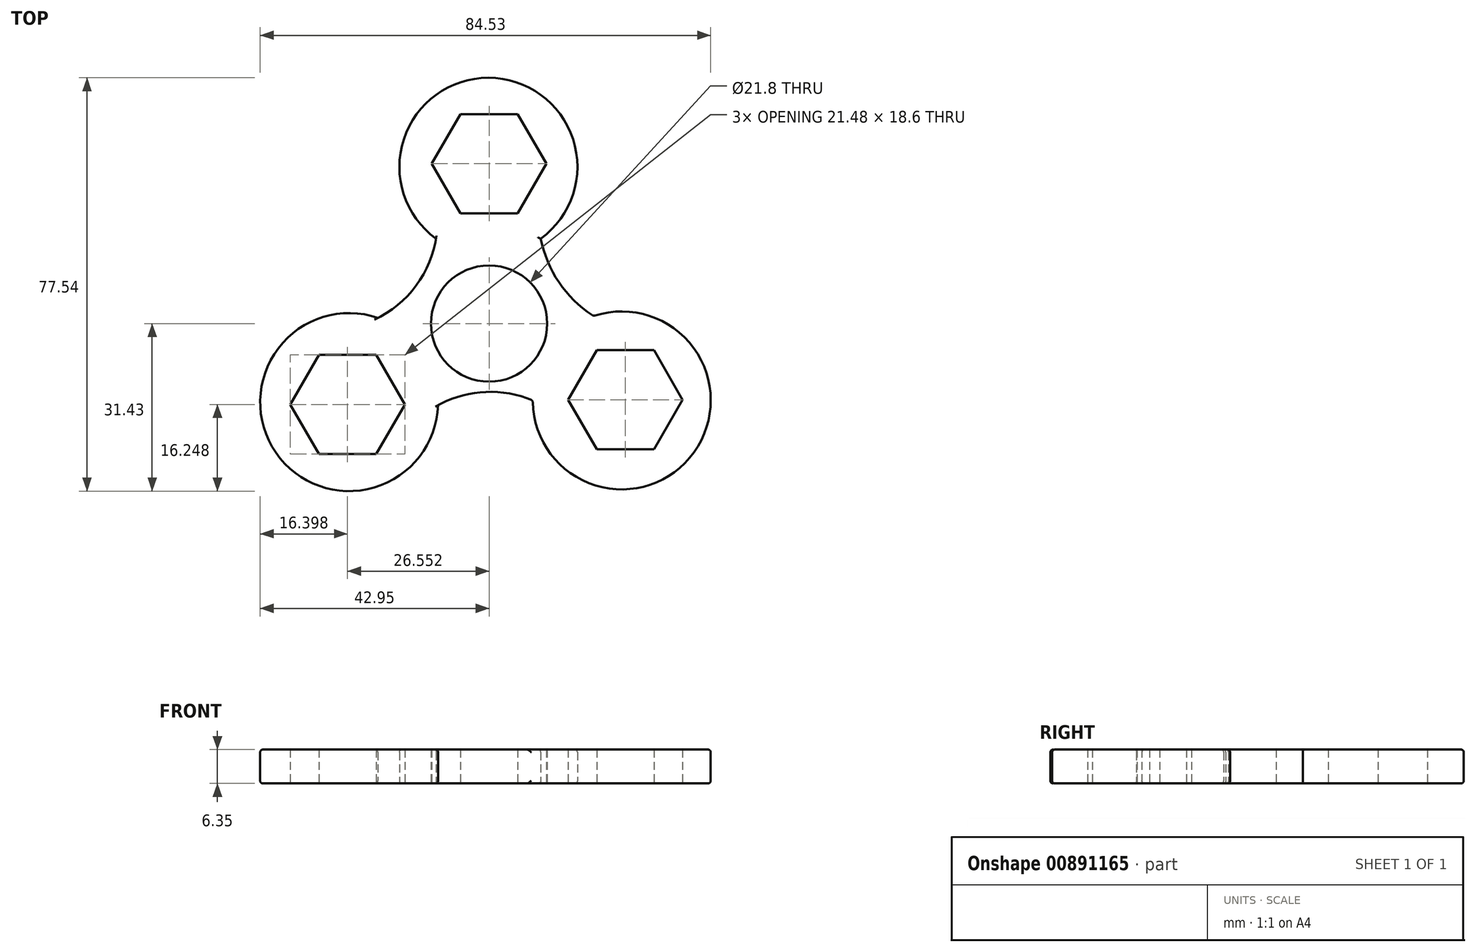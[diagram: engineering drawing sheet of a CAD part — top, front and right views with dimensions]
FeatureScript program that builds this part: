
annotation { "Feature Type Name" : "Feature", "Feature Type Description" : "" }
export const myFeature = defineFeature(function(context is Context, id is Id, definition is map)
    precondition{}
    {
        {
            var Q0;
            Q0=qCreatedBy(makeId("Top.planeOp"),FACE);
            var sketch = newSketch(context, id + "F0", { "sketchPlane" : qUnion([Q0])});
            skCircle(sketch, "E0", {"center": v(0, 0) * mm, "radius": 10.9 * mm});
            skLineSegment(sketch, "E1", {"start": v(0, 0) * mm, "end": v(0, 30) * mm, "construction": true});
            skCircle(sketch, "E2.cCircle", {"center": v(0, 30) * mm, "radius": 9.3 * mm, "construction": true});
            skLineSegment(sketch, "E2.0", {"start": v(5.37, 20.7) * mm, "end": v(-5.37, 20.7) * mm});
            skLineSegment(sketch, "E2.1", {"start": v(-5.37, 20.7) * mm, "end": v(-10.74, 30) * mm});
            skLineSegment(sketch, "E2.2", {"start": v(-10.74, 30) * mm, "end": v(-5.37, 39.3) * mm});
            skLineSegment(sketch, "E2.3", {"start": v(-5.37, 39.3) * mm, "end": v(5.37, 39.3) * mm});
            skLineSegment(sketch, "E2.4", {"start": v(5.37, 39.3) * mm, "end": v(10.74, 30) * mm});
            skLineSegment(sketch, "E2.5", {"start": v(10.74, 30) * mm, "end": v(5.37, 20.7) * mm});
            skPoint(sketch, "E2.0.midPoint", {"position": v(0, 20.7) * mm});
            skCircle(sketch, "E3", {"center": v(0, 0) * mm, "radius": 13.22 * mm, "construction": true});
            skCircle(sketch, "E4.1.0", {"center": v(-26.55, -15.18) * mm, "radius": 9.3 * mm, "construction": true});
            skLineSegment(sketch, "E4.1.1", {"start": v(-31.92, -5.88) * mm, "end": v(-21.18, -5.88) * mm});
            skLineSegment(sketch, "E4.1.2", {"start": v(-15.81, -15.18) * mm, "end": v(-21.18, -24.48) * mm});
            skLineSegment(sketch, "E4.1.3", {"start": v(-21.18, -24.48) * mm, "end": v(-31.92, -24.48) * mm});
            skLineSegment(sketch, "E4.1.4", {"start": v(-37.3, -15.18) * mm, "end": v(-31.92, -5.88) * mm});
            skLineSegment(sketch, "E4.1.5", {"start": v(-21.18, -5.88) * mm, "end": v(-15.81, -15.18) * mm});
            skPoint(sketch, "E4.1.6", {"position": v(-18.5, -10.53) * mm});
            skLineSegment(sketch, "E4.1.7", {"start": v(-31.92, -24.48) * mm, "end": v(-37.3, -15.18) * mm});
            skCircle(sketch, "E4.2.0", {"center": v(25.57, -14.28) * mm, "radius": 9.3 * mm, "construction": true});
            skLineSegment(sketch, "E4.2.1", {"start": v(20.2, -23.58) * mm, "end": v(14.83, -14.28) * mm});
            skLineSegment(sketch, "E4.2.2", {"start": v(20.2, -4.98) * mm, "end": v(30.94, -4.98) * mm});
            skLineSegment(sketch, "E4.2.3", {"start": v(30.94, -4.98) * mm, "end": v(36.3, -14.28) * mm});
            skLineSegment(sketch, "E4.2.4", {"start": v(30.94, -23.58) * mm, "end": v(20.2, -23.58) * mm});
            skLineSegment(sketch, "E4.2.5", {"start": v(14.83, -14.28) * mm, "end": v(20.2, -4.98) * mm});
            skPoint(sketch, "E4.2.6", {"position": v(17.51, -9.63) * mm});
            skLineSegment(sketch, "E4.2.7", {"start": v(36.3, -14.28) * mm, "end": v(30.94, -23.58) * mm});
            skPoint(sketch, "E4.center", {"position": v(0, -0.66) * mm});
            skArc(sketch, "E5", {"start": v(9.7, 15.92) * mm, "mid": v(-0.13, 46.11) * mm, "end": v(-9.97, 15.92) * mm});
            skArc(sketch, "E6", {"start": v(-20.84, 1.06) * mm, "mid": v(-39.93, -24.31) * mm, "end": v(-9.56, -15.06) * mm});
            skArc(sketch, "E7", {"start": v(8.18, -14.43) * mm, "mid": v(38.44, -24.17) * mm, "end": v(19.58, 1.42) * mm});
            skArc(sketch, "E8", {"start": v(9.7, 15.92) * mm, "mid": v(13.17, 7.66) * mm, "end": v(19.58, 1.42) * mm});
            skArc(sketch, "E9", {"start": v(-20.84, 1.06) * mm, "mid": v(-13.64, 7.2) * mm, "end": v(-9.97, 15.92) * mm});
            skArc(sketch, "E10", {"start": v(8.18, -14.43) * mm, "mid": v(-1.15, -12.86) * mm, "end": v(-10.2, -15.65) * mm});
            skSolve(sketch);
        }
        {
            var Q0;
            Q0 = qSketchRegion(id + "F0", true);
            extrude(context, id + "F1", {"entities" : qUnion([Q0]), "depth" : 6.35 * mm, "offsetDistance" : 25 * mm});
        }
        {
            var Q0;
            Q0=makeQuery(id+"F1.opExtrude","CAP_EDGE",EDGE,{"disambiguationData":[OSD([sQuery(id+"F0.wireOp",EDGE,"E7")])],"isStart":false});
            var Q1;
            Q1=makeQuery(id+"F1.opExtrude","CAP_EDGE",EDGE,{"disambiguationData":[OSD([sQuery(id+"F0.wireOp",EDGE,"813a1238-b248-42d5-91d7-d13a114eef2f")])],"isStart":false});
            var Q2;
            Q2=makeQuery(id+"F1.opExtrude","CAP_EDGE",EDGE,{"disambiguationData":[OSD([sQuery(id+"F0.wireOp",EDGE,"E6")])],"isStart":false});
            var Q3;
            Q3=makeQuery(id+"F1.opExtrude","CAP_EDGE",EDGE,{"disambiguationData":[OSD([sQuery(id+"F0.wireOp",EDGE,"ae333e82-591e-45dd-a85c-f704965653f5")])],"isStart":false});
            var Q4;
            Q4=makeQuery(id+"F1.opExtrude","CAP_EDGE",EDGE,{"disambiguationData":[OSD([sQuery(id+"F0.wireOp",EDGE,"E5")])],"isStart":false});
            var Q5;
            Q5=makeQuery(id+"F1.opExtrude","CAP_EDGE",EDGE,{"disambiguationData":[OSD([sQuery(id+"F0.wireOp",EDGE,"E5")])],"isStart":true});
            var Q6;
            Q6=makeQuery(id+"F1.opExtrude","CAP_EDGE",EDGE,{"disambiguationData":[OSD([sQuery(id+"F0.wireOp",EDGE,"E8")])],"isStart":false});
            var Q7;
            Q7=makeQuery(id+"F1.opExtrude","CAP_EDGE",EDGE,{"disambiguationData":[OSD([sQuery(id+"F0.wireOp",EDGE,"813a1238-b248-42d5-91d7-d13a114eef2f")])],"isStart":true});
            var Q8;
            Q8=makeQuery(id+"F1.opExtrude","CAP_EDGE",EDGE,{"disambiguationData":[OSD([sQuery(id+"F0.wireOp",EDGE,"E6")])],"isStart":true});
            var Q9;
            Q9=makeQuery(id+"F1.opExtrude","SWEPT_FACE",FACE,{"disambiguationData":[OSD([sQuery(id+"F0.wireOp",EDGE,"E7")])]});
            var Q10;
            Q10=makeQuery(id+"F1.opExtrude","CAP_EDGE",EDGE,{"disambiguationData":[OSD([sQuery(id+"F0.wireOp",EDGE,"ae333e82-591e-45dd-a85c-f704965653f5")])],"isStart":true});
            var Q11;
            Q11=makeQuery(id+"F1.opExtrude","CAP_EDGE",EDGE,{"disambiguationData":[OSD([sQuery(id+"F0.wireOp",EDGE,"E8")])],"isStart":true});
            fillet(context, id + "F2", {"entities" : qUnion([Q0, Q1, Q2, Q3, Q4, Q5, Q6, Q7, Q8, Q9, Q10, Q11]), "radius" : 0.5 * mm, "tangentPropagation" : true, "allowEdgeOverflow" : false});
        }
    });
